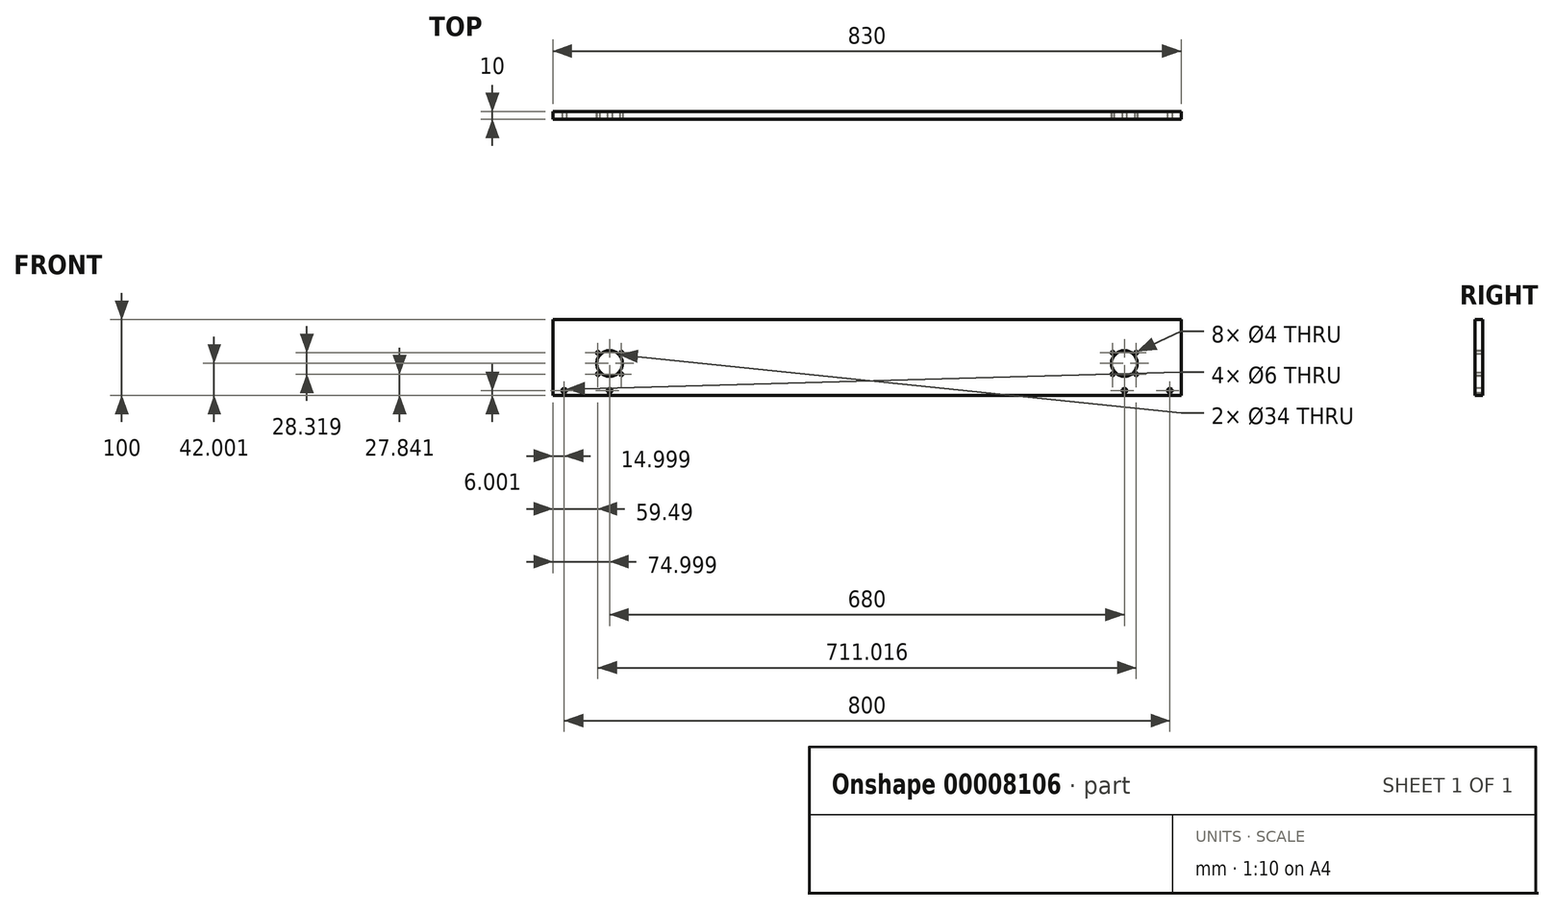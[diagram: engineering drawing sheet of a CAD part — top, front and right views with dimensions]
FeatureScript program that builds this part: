
annotation { "Feature Type Name" : "Feature", "Feature Type Description" : "" }
export const myFeature = defineFeature(function(context is Context, id is Id, definition is map)
    precondition{}
    {
        {
            var Q0;
            Q0=qCreatedBy(makeId("Front.planeOp"),FACE);
            var sketch = newSketch(context, id + "F0", { "sketchPlane" : qUnion([Q0])});
            skLineSegment(sketch, "E0", {"start": v(-312.85, 46.12) * mm, "end": v(-312.85, -53.88) * mm});
            skLineSegment(sketch, "E1", {"start": v(-312.85, -53.88) * mm, "end": v(517.15, -53.88) * mm});
            skLineSegment(sketch, "E2", {"start": v(517.15, -53.88) * mm, "end": v(517.15, 46.12) * mm});
            skLineSegment(sketch, "E3", {"start": v(517.15, 46.12) * mm, "end": v(-312.85, 46.12) * mm});
            skCircle(sketch, "E4", {"center": v(-237.85, -11.88) * mm, "radius": 17 * mm});
            skCircle(sketch, "E5", {"center": v(-253.36, 2.28) * mm, "radius": 2 * mm});
            skCircle(sketch, "E6", {"center": v(-222.34, 2.28) * mm, "radius": 2 * mm});
            skCircle(sketch, "E7", {"center": v(-253.36, -26.04) * mm, "radius": 2 * mm});
            skCircle(sketch, "E8", {"center": v(-222.34, -26.04) * mm, "radius": 2 * mm});
            skCircle(sketch, "E9", {"center": v(-297.85, -47.88) * mm, "radius": 3 * mm});
            skCircle(sketch, "E10", {"center": v(-237.85, -47.88) * mm, "radius": 3 * mm});
            skCircle(sketch, "E11.0.MirrorC", {"center": v(457.66, 2.28) * mm, "radius": 2 * mm});
            skCircle(sketch, "E11.1.MirrorC", {"center": v(426.64, -26.04) * mm, "radius": 2 * mm});
            skCircle(sketch, "E11.2.MirrorC", {"center": v(502.15, -47.88) * mm, "radius": 3 * mm});
            skCircle(sketch, "E11.3.MirrorC", {"center": v(426.64, 2.28) * mm, "radius": 2 * mm});
            skCircle(sketch, "E11.4.MirrorC", {"center": v(442.15, -47.88) * mm, "radius": 3 * mm});
            skCircle(sketch, "E11.5.MirrorC", {"center": v(457.66, -26.04) * mm, "radius": 2 * mm});
            skCircle(sketch, "E11.6.MirrorC", {"center": v(442.15, -11.88) * mm, "radius": 17 * mm});
            skSolve(sketch);
        }
        {
            var Q0;
            Q0=makeQuery(id+"F0.imprint","IMPRINT",FACE,{"disambiguationData":[TD([[makeQuery(id+"F0.imprint","IMPRINT",EDGE,{"derivedFrom":sQuery(id+"F0.wireOp",EDGE,"E0")}),1.0]])]});
            extrude(context, id + "F1", {"entities" : qUnion([Q0]), "oppositeDirection" : true, "depth" : 10 * mm});
        }
    });
